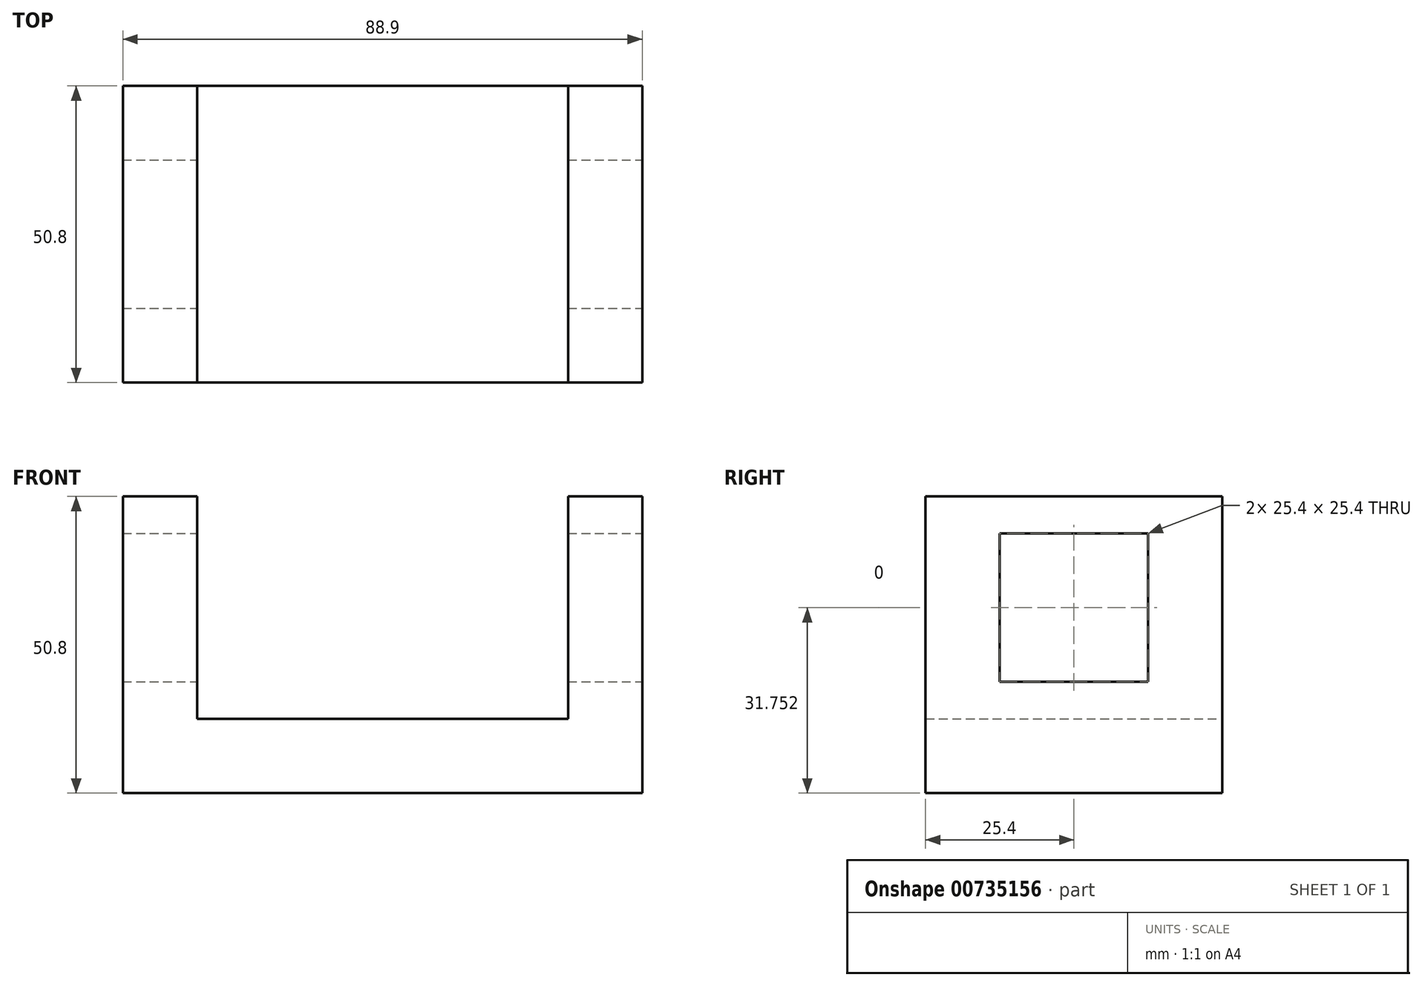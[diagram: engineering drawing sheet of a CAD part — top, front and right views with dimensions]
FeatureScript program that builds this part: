
annotation { "Feature Type Name" : "Feature", "Feature Type Description" : "" }
export const myFeature = defineFeature(function(context is Context, id is Id, definition is map)
    precondition{}
    {
        {
            var Q0;
            Q0=qCreatedBy(makeId("Front.planeOp"),FACE);
            var sketch = newSketch(context, id + "F0", { "sketchPlane" : qUnion([Q0])});
            skLineSegment(sketch, "E0", {"start": v(-42.5, 28.5) * mm, "end": v(-42.5, -22.3) * mm});
            skLineSegment(sketch, "E1", {"start": v(-42.5, -22.3) * mm, "end": v(46.4, -22.3) * mm});
            skLineSegment(sketch, "E2", {"start": v(46.4, -22.3) * mm, "end": v(46.4, 28.5) * mm});
            skLineSegment(sketch, "E3", {"start": v(46.4, 28.5) * mm, "end": v(33.7, 28.5) * mm});
            skLineSegment(sketch, "E4", {"start": v(33.7, 28.5) * mm, "end": v(33.7, -9.6) * mm});
            skLineSegment(sketch, "E5", {"start": v(33.7, -9.6) * mm, "end": v(-29.8, -9.6) * mm});
            skLineSegment(sketch, "E6", {"start": v(-29.8, -9.6) * mm, "end": v(-29.8, 28.5) * mm});
            skLineSegment(sketch, "E7", {"start": v(-29.8, 28.5) * mm, "end": v(-42.5, 28.5) * mm});
            skSolve(sketch);
        }
        {
            var Q0;
            Q0 = qSketchRegion(id + "F0", true);
            extrude(context, id + "F1", {"entities" : qUnion([Q0]), "depth" : 50.8 * mm, "offsetDistance" : 25.4 * mm});
        }
        {
            var Q0;
            Q0=makeQuery(id+"F1.opExtrude","SWEPT_FACE",FACE,{"disambiguationData":[OSD([sQuery(id+"F0.wireOp",EDGE,"E2")])]});
            var sketch = newSketch(context, id + "F2", { "sketchPlane" : qUnion([Q0])});
            skLineSegment(sketch, "E8", {"start": v(-38.1, 22.14) * mm, "end": v(-38.1, -3.26) * mm});
            skLineSegment(sketch, "E9", {"start": v(-38.1, -3.26) * mm, "end": v(-12.7, -3.26) * mm});
            skLineSegment(sketch, "E10", {"start": v(-12.7, -3.26) * mm, "end": v(-12.7, 22.14) * mm});
            skLineSegment(sketch, "E11", {"start": v(-12.7, 22.14) * mm, "end": v(-38.1, 22.14) * mm});
            skSolve(sketch);
        }
        {
            var Q0;
            Q0=makeQuery(id+"F2.imprint","IMPRINT",FACE,{"disambiguationData":[TD([[makeQuery(id+"F2.imprint","IMPRINT",EDGE,{"derivedFrom":sQuery(id+"F2.wireOp",EDGE,"E8")}),1.0]])]});
            extrude(context, id + "F3", {"entities" : qUnion([Q0]), "operationType" : NewBodyOperationType.REMOVE, "endBound" : BoundingType.THROUGH_ALL, "oppositeDirection" : true, "depth" : 12.7 * mm, "offsetDistance" : 25.4 * mm});
        }
    });
